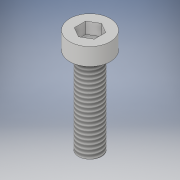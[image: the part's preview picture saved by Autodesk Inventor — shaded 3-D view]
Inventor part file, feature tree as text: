
AUTODESK INVENTOR PART (.ipt)
format: ipt  version: 2019 (Build 230136000, 136)  size: 120,320 bytes
history: native  units: mm
features: extrude x3, sketch x3, other x2
ambient origin geometry x8: Origin, YZ Plane, XZ Plane, XY Plane, X Axis, Y Axis, Z Axis, Center Point
bodies: Body1 (feature_tree)
feature tree (8):
  other  "實體1"
  extrude  "擠出1"  Depth=4.0mm
  extrude  "擠出2"  Depth=15.0mm TaperAngle=0.0deg
  extrude  "擠出3"  Depth=7.0mm
  other  "螺紋1"
  sketch  "草圖1"
  sketch  "草圖2"
  sketch  "草圖3"
